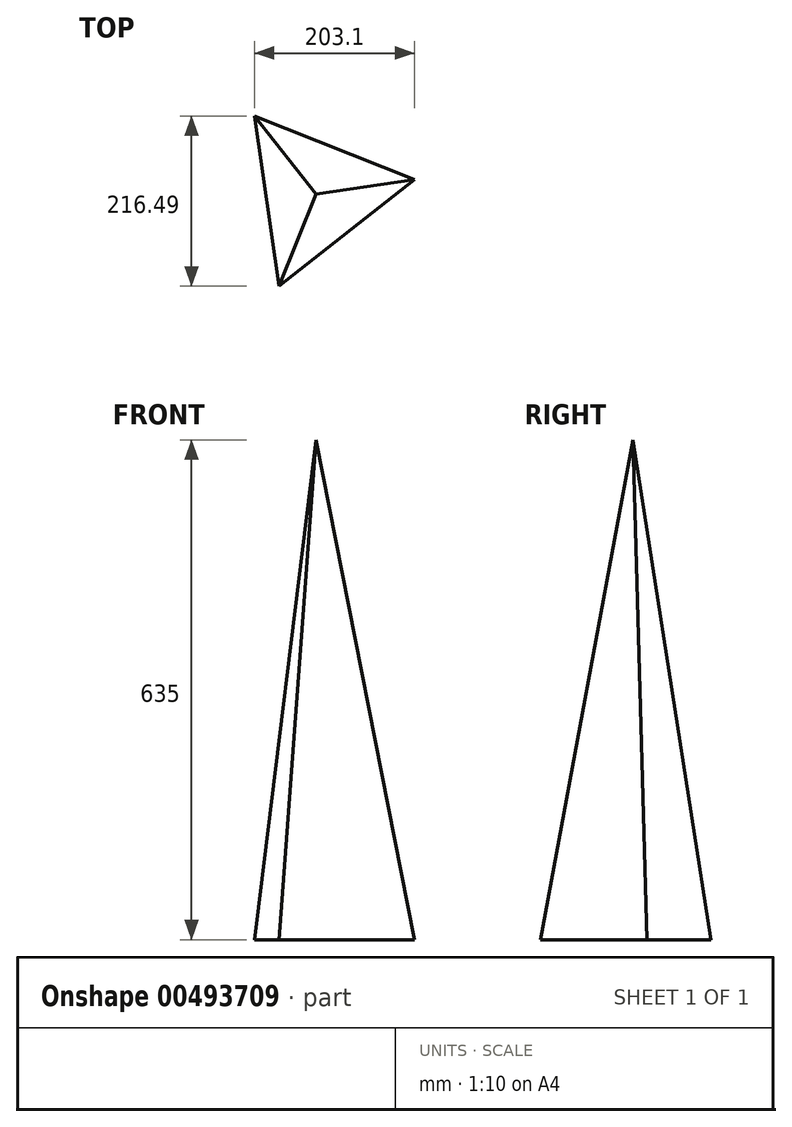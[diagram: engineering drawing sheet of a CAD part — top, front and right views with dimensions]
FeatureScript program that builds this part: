
annotation { "Feature Type Name" : "Feature", "Feature Type Description" : "" }
export const myFeature = defineFeature(function(context is Context, id is Id, definition is map)
    precondition{}
    {
        {
            var Q0;
            Q0=qCreatedBy(makeId("Top.planeOp"),FACE);
            var sketch = newSketch(context, id + "F0", { "sketchPlane" : qUnion([Q0])});
            skCircle(sketch, "E0.cCircle", {"center": v(0, 0) * mm, "radius": 126.28 * mm, "construction": true});
            skLineSegment(sketch, "E0.0", {"start": v(-78.1, 99.23) * mm, "end": v(125, 18.03) * mm});
            skLineSegment(sketch, "E0.1", {"start": v(125, 18.03) * mm, "end": v(-46.88, -117.26) * mm});
            skLineSegment(sketch, "E0.2", {"start": v(-46.88, -117.26) * mm, "end": v(-78.1, 99.23) * mm});
            skSolve(sketch);
        }
        {
            var Q0;
            Q0=qCreatedBy(makeId("Top.planeOp"),FACE);
            cPlane(context, id + "F1", {"entities" : qUnion([Q0]), "cplaneType" : CPlaneType.OFFSET, "offset" : 635 * mm, "width" : 152.4 * mm, "height" : 152.4 * mm});
        }
        {
            var Q0;
            Q0=qCreatedBy(id+"F1.planeOp",FACE);
            var sketch = newSketch(context, id + "F2", { "sketchPlane" : qUnion([Q0])});
            skPoint(sketch, "E1", {"position": v(0, 0) * mm});
            skSolve(sketch);
        }
        {
            var Q0;
            Q0=makeQuery(id+"F0.imprint","IMPRINT",FACE,{"disambiguationData":[TD([[makeQuery(id+"F0.imprint","IMPRINT",EDGE,{"derivedFrom":sQuery(id+"F0.wireOp",EDGE,"E0.0")}),-1.0]])]});
            var Q1;
            Q1=sQuery(id+"F2.wireOp",VERTEX,"E1");
            loft(context, id + "F3", {"sheetProfilesArray" : [{ "sheetProfileEntities" : qUnion([Q0]) }, { "sheetProfileEntities" : qUnion([Q1]) }]});
        }
    });
